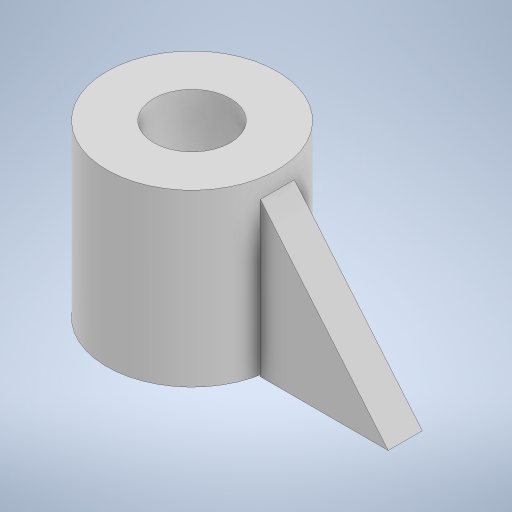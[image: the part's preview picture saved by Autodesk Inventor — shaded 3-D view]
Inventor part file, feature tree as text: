
AUTODESK INVENTOR PART (.ipt)
format: ipt  version: 2023.2 (Build 272271030, 271C)  size: 234,496 bytes
history: native  units: mm
features: extrude x4, sketch x3, plane x1, projected_geometry x1
ambient origin geometry x8: Origin, YZ Plane, XZ Plane, XY Plane, X Axis, Y Axis, Z Axis, Center Point
bodies: Solid1 (feature_tree)
feature tree (9):
  sketch  "Sketch1"  dims[d0=9.0mm d1=20.0mm]
  extrude  "Extrusion1"  Depth=20.0mm
  extrude  "Extrusion2"  Depth=16.0mm TaperAngle=0.0deg
  extrude  "Extrusion3"  Depth=4.0mm
  plane  "Work Plane1"
  extrude  "Extrusion4"  Depth=4.0mm TaperAngle=0.0deg
  sketch  "Sketch2"  dims[d2=20.0mm d3=0.0mm d4=16.0mm d5=0.0mm]
  projected_geometry  "Projected Loop1"
  sketch  "Sketch3"  dims[d6=15.0mm d7=18.0mm d8=4.0mm d9=0.0mm d10=-16.0mm d11=5.5mm d12=0.0mm d13=0.0mm]
